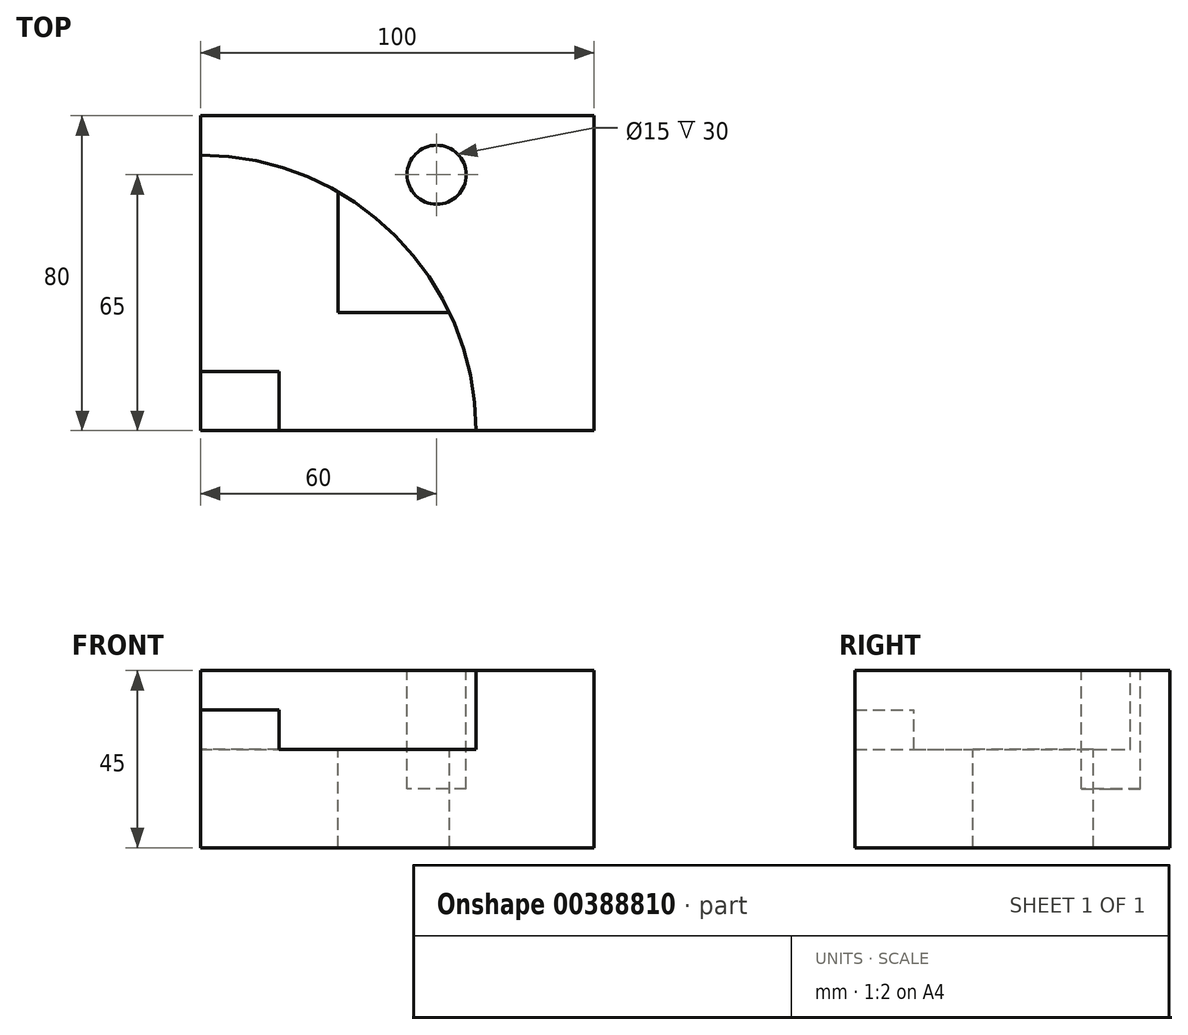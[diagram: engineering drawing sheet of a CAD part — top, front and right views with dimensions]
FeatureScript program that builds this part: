
annotation { "Feature Type Name" : "Feature", "Feature Type Description" : "" }
export const myFeature = defineFeature(function(context is Context, id is Id, definition is map)
    precondition{}
    {
        {
            var Q0;
            Q0=qCreatedBy(makeId("Front.planeOp"),FACE);
            var sketch = newSketch(context, id + "F0", { "sketchPlane" : qUnion([Q0])});
            skLineSegment(sketch, "E0.bottom", {"start": v(0, 0) * mm, "end": v(-100, 0) * mm});
            skLineSegment(sketch, "E0.top", {"start": v(0, 45) * mm, "end": v(-100, 45) * mm});
            skLineSegment(sketch, "E0.left", {"start": v(0, 0) * mm, "end": v(0, 45) * mm});
            skLineSegment(sketch, "E0.right", {"start": v(-100, 0) * mm, "end": v(-100, 45) * mm});
            skSolve(sketch);
        }
        {
            var Q0;
            Q0=makeQuery(id+"F0.imprint","IMPRINT",FACE,{"disambiguationData":[TD([[makeQuery(id+"F0.imprint","IMPRINT",EDGE,{"derivedFrom":sQuery(id+"F0.wireOp",EDGE,"E0.bottom")}),-1.0]])]});
            extrude(context, id + "F1", {"entities" : qUnion([Q0]), "depth" : 80 * mm});
        }
        {
            var Q0;
            Q0=makeQuery(id+"F1.opExtrude","SWEPT_FACE",FACE,{"disambiguationData":[OSD([sQuery(id+"F0.wireOp",EDGE,"E0.top")])]});
            var sketch = newSketch(context, id + "F2", { "sketchPlane" : qUnion([Q0])});
            skLineSegment(sketch, "E1", {"start": v(-100, 0) * mm, "end": v(-40, 0) * mm});
            skLineSegment(sketch, "E2", {"start": v(-40, 0) * mm, "end": v(-40, -15) * mm});
            skCircle(sketch, "E3", {"center": v(-40, -15) * mm, "radius": 7.5 * mm});
            skSolve(sketch);
        }
        {
            var Q0;
            Q0=makeQuery(id+"F2.imprint","IMPRINT",FACE,{"disambiguationData":[TD([[makeQuery(id+"F2.imprint","IMPRINT",EDGE,{"derivedFrom":sQuery(id+"F2.wireOp",EDGE,"E3")}),1.0]])]});
            extrude(context, id + "F3", {"entities" : qUnion([Q0]), "operationType" : NewBodyOperationType.REMOVE, "oppositeDirection" : true, "depth" : 30 * mm});
        }
        {
            var Q0;
            Q0=makeQuery(id+"F1.opExtrude","SWEPT_FACE",FACE,{"disambiguationData":[OSD([sQuery(id+"F0.wireOp",EDGE,"E0.top")])]});
            var sketch = newSketch(context, id + "F4", { "sketchPlane" : qUnion([Q0])});
            skCircle(sketch, "E4", {"center": v(-100, -80) * mm, "radius": 70 * mm});
            skLineSegment(sketch, "E5.bottom", {"start": v(-100, -80) * mm, "end": v(-80, -80) * mm});
            skLineSegment(sketch, "E5.top", {"start": v(-100, -65) * mm, "end": v(-80, -65) * mm});
            skLineSegment(sketch, "E5.left", {"start": v(-100, -80) * mm, "end": v(-100, -65) * mm});
            skLineSegment(sketch, "E5.right", {"start": v(-80, -80) * mm, "end": v(-80, -65) * mm});
            skLineSegment(sketch, "E6", {"start": v(-57.37, -50) * mm, "end": v(-36.75, -50) * mm});
            skLineSegment(sketch, "E7", {"start": v(-65, -49.37) * mm, "end": v(-65, -19.38) * mm});
            skLineSegment(sketch, "E8", {"start": v(-65, -49.37) * mm, "end": v(-65, -50) * mm});
            skLineSegment(sketch, "E9", {"start": v(-65, -50) * mm, "end": v(-57.37, -50) * mm});
            skSolve(sketch);
        }
        {
            var Q0;
            {var subQ1=sQuery(id+"F4.wireOp",EDGE,"E6");Q0=makeQuery(id+"F4.imprint","IMPRINT",FACE,{"disambiguationData":[TD([[makeQuery(id+"F4.imprint","IMPRINT",EDGE,{"derivedFrom":subQ1}),1.0]])]});}
            extrude(context, id + "F5", {"entities" : qUnion([Q0]), "operationType" : NewBodyOperationType.REMOVE, "endBound" : BoundingType.THROUGH_ALL, "oppositeDirection" : true, "depth" : 25 * mm});
        }
        {
            var Q0;
            {var subQ8=sQuery(id+"F4.wireOp",EDGE,"E5.top");Q0=makeQuery(id+"F4.imprint","IMPRINT",FACE,{"disambiguationData":[TD([[makeQuery(id+"F4.imprint","IMPRINT",EDGE,{"derivedFrom":subQ8}),1.0]])]});}
            extrude(context, id + "F6", {"entities" : qUnion([Q0]), "operationType" : NewBodyOperationType.REMOVE, "oppositeDirection" : true, "depth" : 20 * mm});
        }
        {
            var Q0;
            Q0=makeQuery(id+"F4.imprint","IMPRINT",FACE,{"disambiguationData":[TD([[makeQuery(id+"F4.imprint","IMPRINT",EDGE,{"derivedFrom":sQuery(id+"F4.wireOp",EDGE,"E5.bottom")}),-1.0]])]});
            extrude(context, id + "F7", {"entities" : qUnion([Q0]), "operationType" : NewBodyOperationType.REMOVE, "oppositeDirection" : true, "depth" : 10 * mm});
        }
    });
